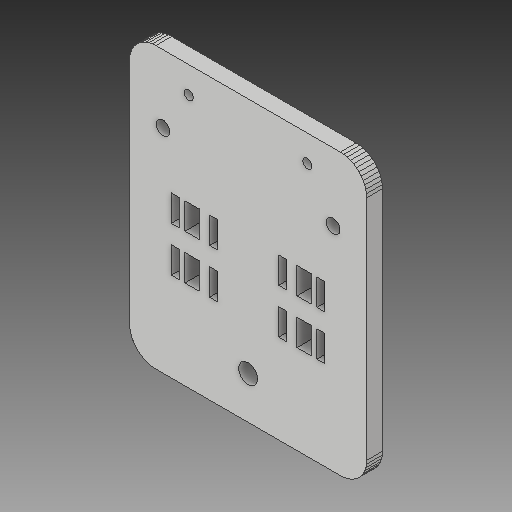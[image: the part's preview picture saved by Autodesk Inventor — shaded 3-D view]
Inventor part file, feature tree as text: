
AUTODESK INVENTOR PART (.ipt)
format: ipt  version: 2018 (Build 220112000, 112)  size: 313,344 bytes
history: native  units: mm
features: sketch x4, other x3
ambient origin geometry x8: Origin, YZ Plane, XZ Plane, XY Plane, X Axis, Y Axis, Z Axis, Center Point
bodies: Solid1 (feature_tree)
feature tree (7):
  other  "X-Axis-End-Plate.ipt"
  other  "Solid1::X-Axis-End-Plate.ipt"
  other  "TaggingFeature1"
  sketch  "Sketch1"  dims[d0=10.0mm]
  sketch  "Sketch2"
  sketch  "Sketch3"
  sketch  "Sketch4"
